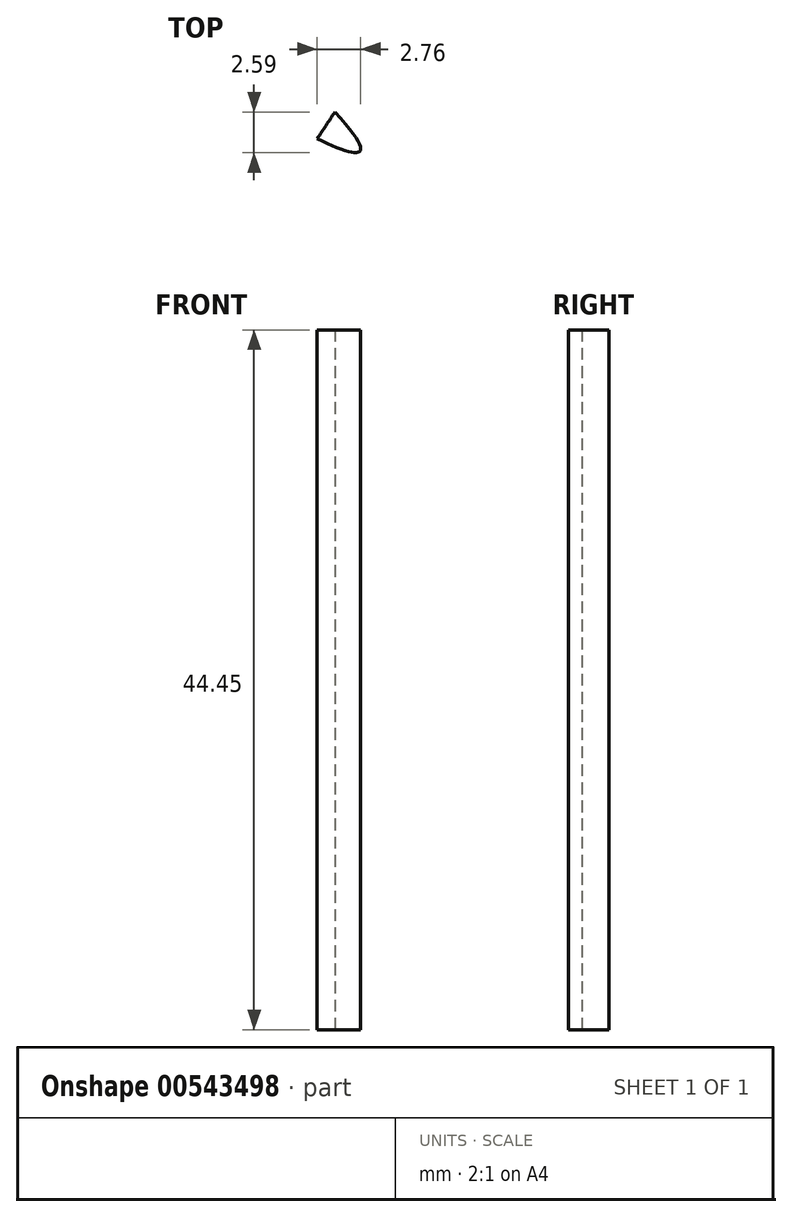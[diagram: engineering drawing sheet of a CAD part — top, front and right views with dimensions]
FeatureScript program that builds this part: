
annotation { "Feature Type Name" : "Feature", "Feature Type Description" : "" }
export const myFeature = defineFeature(function(context is Context, id is Id, definition is map)
    precondition{}
    {
        {
            var Q0;
            Q0=qCreatedBy(makeId("Top.planeOp"),FACE);
            var sketch = newSketch(context, id + "F0", { "sketchPlane" : qUnion([Q0])});
            skFitSpline(sketch, "E0", {"points": [v(-82.74, 217.68) * mm, v(-15.01, 218.96) * mm, v(70.61, 166.56) * mm, v(151.13, 206.18) * mm, v(163.9, 240.69) * mm, v(180.52, 249.63) * mm, v(202.25, 226.63) * mm, v(181.8, 115.44) * mm, v(142.18, -20.02) * mm, v(170.3, -122.26) * mm, v(194.58, -223.22) * mm, v(135.8, -282.01) * mm, v(50.17, -294.8) * mm, v(-177.31, -257.73) * mm, v(-211.82, -158.05) * mm, v(-167.1, -76.25) * mm, v(-130.03, -4.69) * mm, v(-121.08, 65.6) * mm, v(-147.92, 148.67) * mm, v(-82.74, 217.68) * mm]});
            skFitSpline(sketch, "E1", {"points": [v(-167.1, -76.25) * mm, v(-176.04, -76.25) * mm], "startDerivative": vector(24.28, -26.84) * mm, "endDerivative": vector(24.28, -26.84) * mm});
            skSolve(sketch);
        }
        {
            var Q0;
            {var subQ0=sQuery(id+"F0.wireOp",EDGE,"E1");var subQ1=sQuery(id+"F0.wireOp",EDGE,"E0");var subQ2=makeQuery(id+"F0.imprint","INTERSECT",VERTEX,{"disambiguationData":[OD(0.0)],"derivedFrom":[subQ1,subQ0]});Q0=makeQuery(id+"F0.imprint","IMPRINT",FACE,{"disambiguationData":[TD([[makeQuery(id+"F0.imprint","IMPRINT",EDGE,{"disambiguationData":[TD([[subQ2,-1.0]])],"derivedFrom":subQ1}),-1.0]])]});}
            extrude(context, id + "F1", {"entities" : qUnion([Q0]), "depth" : 44.45 * mm, "offsetDistance" : 25.4 * mm});
        }
        {
            var Q0;
            Q0=makeQuery(id+"F1.opExtrude","CAP_FACE",FACE,{"disambiguationData":[OSD([sQuery(id+"F0.wireOp",EDGE,"E0"),sQuery(id+"F0.wireOp",EDGE,"E1")])],"isStart":false});
            var sketch = newSketch(context, id + "F2", { "sketchPlane" : qUnion([Q0])});
            skArc(sketch, "E2", {"start": v(-46.13, -122.82) * mm, "mid": v(-63.4, -140.1) * mm, "end": v(-46.13, -157.37) * mm});
            skArc(sketch, "E3", {"start": v(30.13, -157.37) * mm, "mid": v(47.4, -140.1) * mm, "end": v(30.13, -122.82) * mm});
            skLineSegment(sketch, "E4", {"start": v(-46.13, -122.82) * mm, "end": v(30.13, -122.82) * mm});
            skLineSegment(sketch, "E5", {"start": v(-46.13, -157.37) * mm, "end": v(30.13, -157.37) * mm});
            skSolve(sketch);
        }
        {
            var Q0;
            Q0=makeQuery(id+"F2.imprint","IMPRINT",FACE,{"disambiguationData":[TD([[makeQuery(id+"F2.imprint","IMPRINT",EDGE,{"derivedFrom":sQuery(id+"F2.wireOp",EDGE,"E2")}),1.0]])]});
            extrude(context, id + "F3", {"entities" : qUnion([Q0]), "operationType" : NewBodyOperationType.REMOVE, "oppositeDirection" : true, "depth" : 25.4 * mm, "offsetDistance" : 25.4 * mm});
        }
    });
